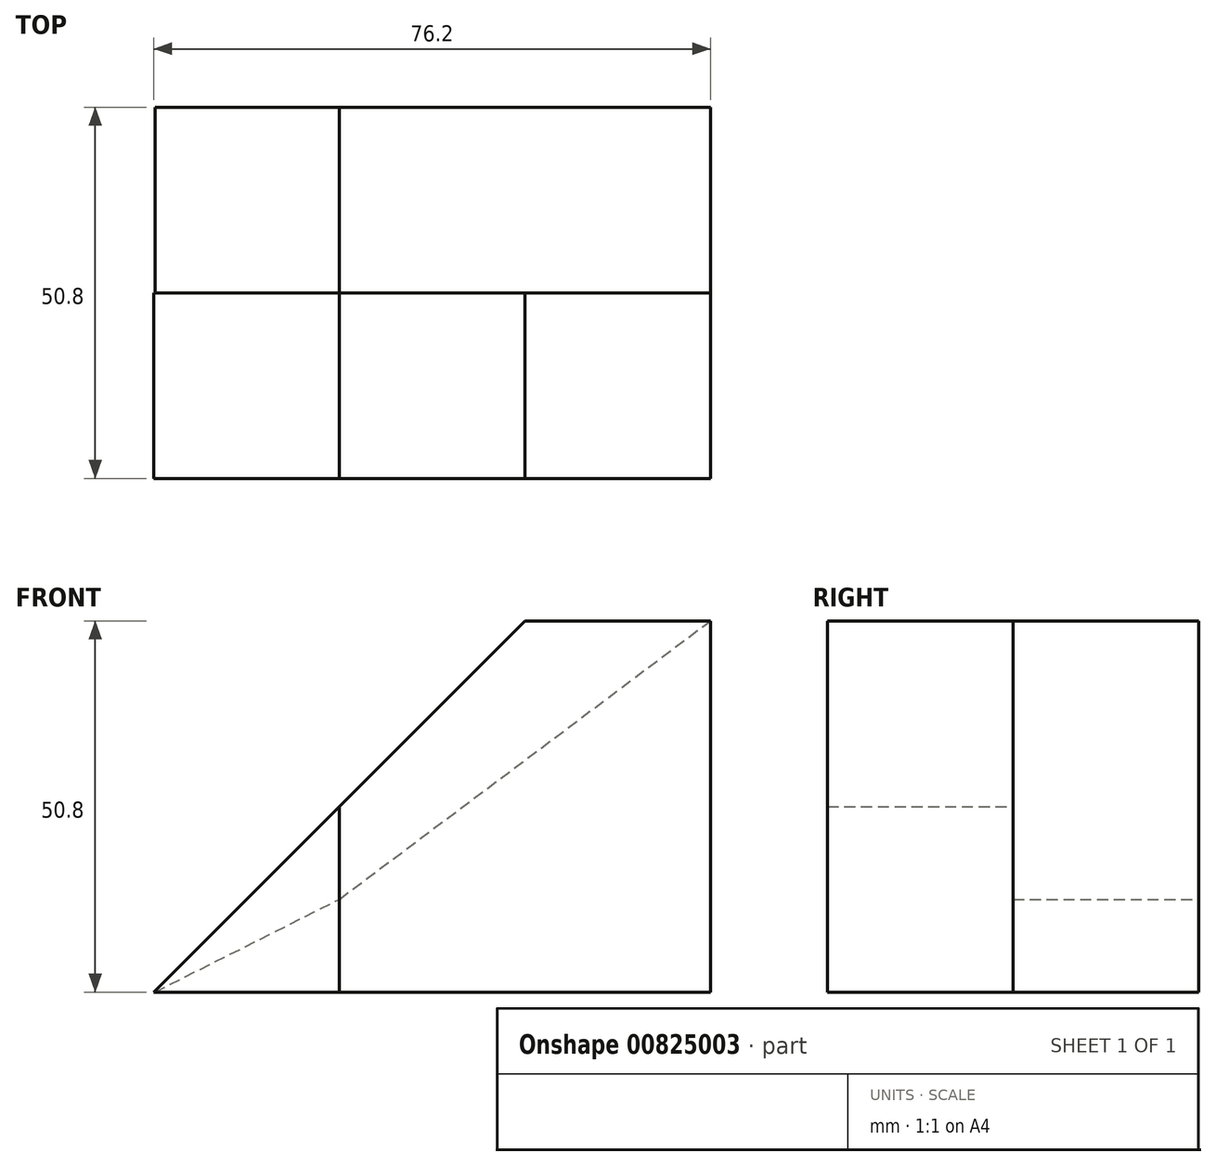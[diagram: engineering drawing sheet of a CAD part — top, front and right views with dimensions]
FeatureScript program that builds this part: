
annotation { "Feature Type Name" : "Feature", "Feature Type Description" : "" }
export const myFeature = defineFeature(function(context is Context, id is Id, definition is map)
    precondition{}
    {
        {
            var Q0;
            Q0=qCreatedBy(makeId("Front.planeOp"),FACE);
            var sketch = newSketch(context, id + "F0", { "sketchPlane" : qUnion([Q0])});
            skLineSegment(sketch, "E0", {"start": v(0, 0) * mm, "end": v(0, -50.8) * mm});
            skLineSegment(sketch, "E1", {"start": v(0, -50.8) * mm, "end": v(-50.8, -50.8) * mm});
            skLineSegment(sketch, "E2", {"start": v(-50.8, -50.8) * mm, "end": v(-50.8, -25.4) * mm});
            skLineSegment(sketch, "E3", {"start": v(0, 0) * mm, "end": v(-25.4, 0) * mm});
            skLineSegment(sketch, "E4", {"start": v(-25.4, 0) * mm, "end": v(-50.8, -25.4) * mm});
            skSolve(sketch);
        }
        {
            var Q0;
            Q0=makeQuery(id+"F0.imprint","IMPRINT",FACE,{"disambiguationData":[TD([[makeQuery(id+"F0.imprint","IMPRINT",EDGE,{"derivedFrom":sQuery(id+"F0.wireOp",EDGE,"E0")}),-1.0]])]});
            extrude(context, id + "F1", {"entities" : qUnion([Q0]), "depth" : 25.4 * mm, "offsetDistance" : 25.4 * mm});
        }
        {
            var Q0;
            Q0=makeQuery(id+"F1.opExtrude","CAP_FACE",FACE,{"disambiguationData":[OSD([sQuery(id+"F0.wireOp",EDGE,"E0"),sQuery(id+"F0.wireOp",EDGE,"E1"),sQuery(id+"F0.wireOp",EDGE,"E2"),sQuery(id+"F0.wireOp",EDGE,"E3"),sQuery(id+"F0.wireOp",EDGE,"E4")])],"isStart":false});
            var sketch = newSketch(context, id + "F2", { "sketchPlane" : qUnion([Q0])});
            skLineSegment(sketch, "E5", {"start": v(0, -50.8) * mm, "end": v(-76.2, -50.8) * mm});
            skLineSegment(sketch, "E6", {"start": v(0, -50.8) * mm, "end": v(0, 0) * mm});
            skLineSegment(sketch, "E7", {"start": v(0, 0) * mm, "end": v(-25.4, 0) * mm});
            skLineSegment(sketch, "E8", {"start": v(-25.4, 0) * mm, "end": v(-25.4, -25.4) * mm});
            skLineSegment(sketch, "E9", {"start": v(-25.4, -25.4) * mm, "end": v(-76.2, -50.8) * mm});
            skLineSegment(sketch, "E10", {"start": v(-76.2, -50.8) * mm, "end": v(-25.4, 0) * mm});
            skSolve(sketch);
        }
        {
            var Q0;
            {var subQ0=sQuery(id+"F2.wireOp",EDGE,"E5");var subQ1=makeQuery(id+"F1.opExtrude","CAP_EDGE",EDGE,{"disambiguationData":[OSD([sQuery(id+"F0.wireOp",EDGE,"E2")])],"isStart":false});var subQ2=makeQuery(id+"F2.imprint","INTERSECT",VERTEX,{"derivedFrom":[subQ1,subQ0]});Q0=makeQuery(id+"F2.imprint","IMPRINT",FACE,{"disambiguationData":[TD([[makeQuery(id+"F2.imprint","IMPRINT",EDGE,{"disambiguationData":[TD([[subQ2,-1.0]])],"derivedFrom":subQ1}),1.0]])]});}
            extrude(context, id + "F3", {"entities" : qUnion([Q0]), "depth" : 25.4 * mm, "offsetDistance" : 25.4 * mm});
        }
        {
            var Q0;
            Q0=makeQuery(id+"F1.opExtrude","CAP_FACE",FACE,{"disambiguationData":[OSD([sQuery(id+"F0.wireOp",EDGE,"E0"),sQuery(id+"F0.wireOp",EDGE,"E1"),sQuery(id+"F0.wireOp",EDGE,"E2"),sQuery(id+"F0.wireOp",EDGE,"E3"),sQuery(id+"F0.wireOp",EDGE,"E4")])],"isStart":false});
            var sketch = newSketch(context, id + "F4", { "sketchPlane" : qUnion([Q0])});
            skLineSegment(sketch, "E11", {"start": v(-50.8, -50.8) * mm, "end": v(0, -50.8) * mm});
            skLineSegment(sketch, "E12", {"start": v(0, -50.8) * mm, "end": v(0, 0) * mm});
            skLineSegment(sketch, "E13", {"start": v(0, 0) * mm, "end": v(-25.4, 0) * mm});
            skLineSegment(sketch, "E14", {"start": v(-25.4, 0) * mm, "end": v(-76.2, -50.8) * mm});
            skLineSegment(sketch, "E15", {"start": v(-76.2, -50.8) * mm, "end": v(-50.8, -38.1) * mm});
            skLineSegment(sketch, "E16", {"start": v(-50.8, -38.1) * mm, "end": v(-50.8, -50.8) * mm});
            skSolve(sketch);
        }
        {
            var Q0;
            {var subQ3=sQuery(id+"F4.wireOp",EDGE,"E15");Q0=makeQuery(id+"F4.imprint","IMPRINT",FACE,{"disambiguationData":[TD([[makeQuery(id+"F4.imprint","IMPRINT",EDGE,{"derivedFrom":subQ3}),1.0]])]});}
            extrude(context, id + "F5", {"entities" : qUnion([Q0]), "operationType" : NewBodyOperationType.ADD, "depth" : 25.4 * mm, "offsetDistance" : 25.4 * mm});
        }
        {
            var Q0;
            Q0=makeQuery(id+"F1.opExtrude","CAP_FACE",FACE,{"disambiguationData":[OSD([sQuery(id+"F0.wireOp",EDGE,"E0"),sQuery(id+"F0.wireOp",EDGE,"E1"),sQuery(id+"F0.wireOp",EDGE,"E2"),sQuery(id+"F0.wireOp",EDGE,"E3"),sQuery(id+"F0.wireOp",EDGE,"E4")])],"isStart":false});
            var sketch = newSketch(context, id + "F6", { "sketchPlane" : qUnion([Q0])});
            skLineSegment(sketch, "E17", {"start": v(-50.8, -25.4) * mm, "end": v(-25.4, 0) * mm});
            skLineSegment(sketch, "E18", {"start": v(-25.4, 0) * mm, "end": v(0, 0) * mm});
            skLineSegment(sketch, "E19", {"start": v(0, 0) * mm, "end": v(0, -50.8) * mm});
            skLineSegment(sketch, "E20", {"start": v(0, -50.8) * mm, "end": v(-50.8, -50.8) * mm});
            skLineSegment(sketch, "E21", {"start": v(-50.8, -50.8) * mm, "end": v(-50.8, -25.4) * mm});
            skSolve(sketch);
        }
        {
            var Q0;
            Q0=makeQuery(id+"F6.imprint","IMPRINT",FACE,{"disambiguationData":[TD([[makeQuery(id+"F6.imprint","IMPRINT",EDGE,{"derivedFrom":sQuery(id+"F6.wireOp",EDGE,"E17")}),1.0]])]});
            extrude(context, id + "F7", {"entities" : qUnion([Q0]), "depth" : 25.4 * mm, "offsetDistance" : 25.4 * mm});
        }
        {
            var Q0;
            Q0=makeQuery(id+"F1.opExtrude","CAP_FACE",FACE,{"disambiguationData":[OSD([sQuery(id+"F0.wireOp",EDGE,"E0"),sQuery(id+"F0.wireOp",EDGE,"E1"),sQuery(id+"F0.wireOp",EDGE,"E2"),sQuery(id+"F0.wireOp",EDGE,"E3"),sQuery(id+"F0.wireOp",EDGE,"E4")])],"isStart":true});
            var sketch = newSketch(context, id + "F8", { "sketchPlane" : qUnion([Q0])});
            skLineSegment(sketch, "E22", {"start": v(50.8, -25.4) * mm, "end": v(50.8, -38.1) * mm});
            skLineSegment(sketch, "E23", {"start": v(50.8, -38.1) * mm, "end": v(50.8, -50.8) * mm});
            skLineSegment(sketch, "E24", {"start": v(50.8, -50.8) * mm, "end": v(76.03, -50.8) * mm});
            skLineSegment(sketch, "E25", {"start": v(76.03, -50.8) * mm, "end": v(50.8, -38.1) * mm});
            skSolve(sketch);
        }
        {
            var Q0;
            Q0=makeQuery(id+"F8.imprint","IMPRINT",FACE,{"disambiguationData":[TD([[makeQuery(id+"F8.imprint","IMPRINT",EDGE,{"derivedFrom":sQuery(id+"F8.wireOp",EDGE,"E23")}),-1.0]])]});
            extrude(context, id + "F9", {"entities" : qUnion([Q0]), "oppositeDirection" : true, "depth" : 25.4 * mm, "offsetDistance" : 25.4 * mm});
        }
        {
            var Q0;
            Q0=makeQuery(id+"F1.opExtrude","CAP_FACE",FACE,{"disambiguationData":[OSD([sQuery(id+"F0.wireOp",EDGE,"E0"),sQuery(id+"F0.wireOp",EDGE,"E1"),sQuery(id+"F0.wireOp",EDGE,"E2"),sQuery(id+"F0.wireOp",EDGE,"E3"),sQuery(id+"F0.wireOp",EDGE,"E4")])],"isStart":true});
            var sketch = newSketch(context, id + "F10", { "sketchPlane" : qUnion([Q0])});
            skLineSegment(sketch, "E26", {"start": v(50.8, -38.1) * mm, "end": v(0, 0) * mm});
            skLineSegment(sketch, "E27", {"start": v(0, 0) * mm, "end": v(25.4, 0) * mm});
            skLineSegment(sketch, "E28", {"start": v(25.4, 0) * mm, "end": v(50.8, -25.4) * mm});
            skLineSegment(sketch, "E29", {"start": v(50.8, -25.4) * mm, "end": v(50.8, -38.1) * mm});
            skSolve(sketch);
        }
        {
            var Q0;
            Q0=makeQuery(id+"F10.imprint","IMPRINT",FACE,{"disambiguationData":[TD([[makeQuery(id+"F10.imprint","IMPRINT",EDGE,{"derivedFrom":sQuery(id+"F10.wireOp",EDGE,"E26")}),-1.0]])]});
            extrude(context, id + "F11", {"entities" : qUnion([Q0]), "operationType" : NewBodyOperationType.REMOVE, "oppositeDirection" : true, "depth" : 25.4 * mm, "offsetDistance" : 25.4 * mm});
        }
    });
